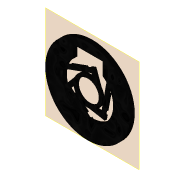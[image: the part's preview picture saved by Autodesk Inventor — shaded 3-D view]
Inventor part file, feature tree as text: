
AUTODESK INVENTOR PART (.ipt)
format: ipt  version: 2022 (Build 260153000, 153)  size: 204,288 bytes
history: native  units: mm
features: other x4, extrude x3, reference x3, sketch x2, projected_geometry x2, plane x1, pattern_circular x1
ambient origin geometry x8: Origin, YZ Plane, XZ Plane, XY Plane, X Axis, Y Axis, Z Axis, Center Point
bodies: Volumenkörper1 (feature_tree)
feature tree (16):
  plane  "Arbeitsebene1"
  extrude  "Extrusion1"  Depth=2.0mm TaperAngle=0.0deg
  extrude  "Extrusion2"  Depth=2.0mm
  extrude  "Extrusion3"  Depth=2.0mm
  pattern_circular  "Runde Anordnung1"  [2 undecoded]
  sketch  "Skizze1"  dims[d0=23.0mm d1=2.0mm d2=0.0mm]
  reference  "Referenz1"
  sketch  "Skizze2"  dims[d3=13.0mm d4=2.0mm d5=2.0mm d6=1.0mm d7=0.0mm d8=2.0mm d9=2.0mm d10=0.7mm d11=0.0mm d15=30.0mm d16=360.0deg d22=0.5mm d23=0.872665mm d24=0.5mm d25=0.872665mm]
  projected_geometry  "Projizierte Kontur1"
  reference  "Referenz2"
  reference  "Referenz3"
  projected_geometry  "Projizierte Kontur2"
  other  "Assembly_ETL_v0.iam"
  other  "50_ETL_Base_v0:1"
  other  "00_Ringmagnet_10x5x3mm:1"
  other  "50_ETL_28by_coil:1"
note: 2 required parameter values undecoded (feature->parameter linkage not recoverable at this tier; creation-order binding heuristic only, values carry confidence <= 0.55)
